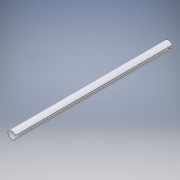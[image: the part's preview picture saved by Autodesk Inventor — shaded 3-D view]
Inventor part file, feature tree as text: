
AUTODESK INVENTOR PART (.ipt)
format: ipt  version: 2017 (Build 210142000, 142)  size: 105,984 bytes
history: native  units: in
note: dims shown in document units (in); Inventor stores cm internally (conversion verified against a paired STEP export)
features: extrude x2, sketch x2
ambient origin geometry x8: Origin, YZ Plane, XZ Plane, XY Plane, X Axis, Y Axis, Z Axis, Center Point
bodies: Solid1 (feature_tree)
feature tree (4):
  extrude  "Extrusion1"  Depth=0.813in
  extrude  "Extrusion4"  Depth=0.4528in
  sketch  "Sketch1"  dims[d0=1.0449in d1=0.813in]
  sketch  "Sketch4"  dims[d2=20.4724in d3=0.0in d9=0.7874in d10=0.4528in d11=0.0in d12=0.0in]
